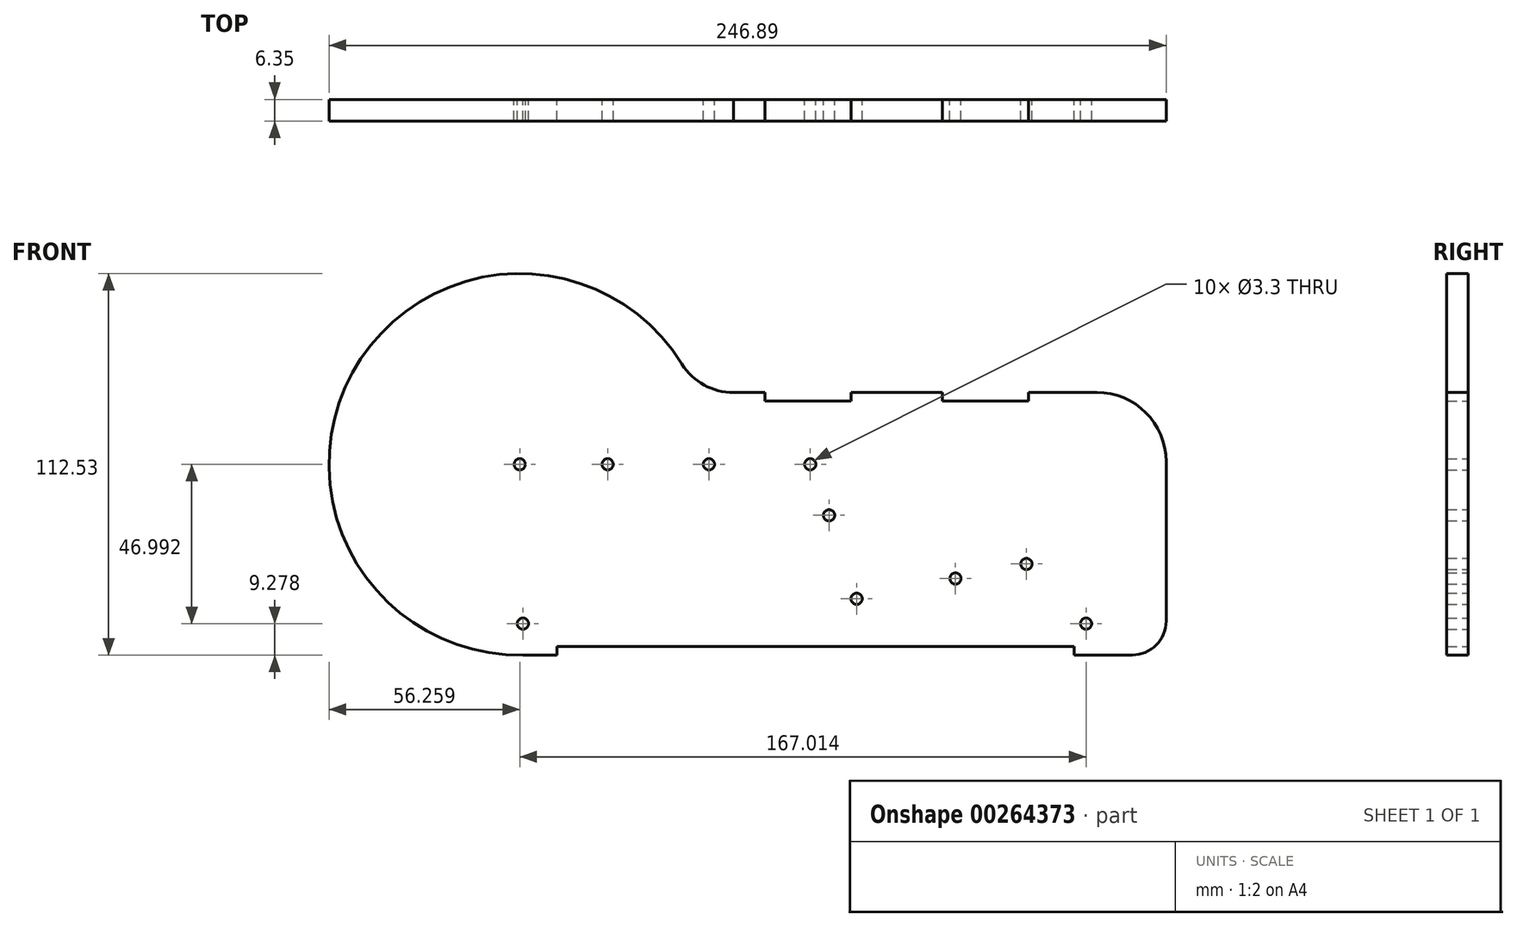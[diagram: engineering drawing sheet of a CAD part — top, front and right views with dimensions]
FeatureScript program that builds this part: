
annotation { "Feature Type Name" : "Feature", "Feature Type Description" : "" }
export const myFeature = defineFeature(function(context is Context, id is Id, definition is map)
    precondition{}
    {
        {
            var Q0;
            Q0=qCreatedBy(makeId("Front.planeOp"),FACE);
            var sketch = newSketch(context, id + "F0", { "sketchPlane" : qUnion([Q0])});
            skCircle(sketch, "E0", {"center": v(-31.53, 0) * mm, "radius": 1.65 * mm});
            skCircle(sketch, "E1", {"center": v(-61.4, 0) * mm, "radius": 1.65 * mm});
            skLineSegment(sketch, "E2.top", {"start": v(-86.4, -56.26) * mm, "end": v(-76.4, -56.26) * mm});
            skLineSegment(sketch, "E2.right", {"start": v(103.3, -10.33) * mm, "end": v(103.3, -46.23) * mm});
            skCircle(sketch, "E3", {"center": v(-87.33, 0) * mm, "radius": 1.65 * mm});
            skCircle(sketch, "E4", {"center": v(-1.66, 0) * mm, "radius": 1.65 * mm});
            skCircle(sketch, "E5", {"center": v(3.89, -15.04) * mm, "radius": 1.65 * mm});
            skCircle(sketch, "E6", {"center": v(41.18, -33.7) * mm, "radius": 1.65 * mm});
            skCircle(sketch, "E7", {"center": v(62.11, -29.4) * mm, "radius": 1.65 * mm});
            skCircle(sketch, "E8", {"center": v(79.68, -47) * mm, "radius": 1.65 * mm});
            skCircle(sketch, "E9", {"center": v(12.02, -39.66) * mm, "radius": 1.65 * mm});
            skLineSegment(sketch, "E10", {"start": v(103.3, -10.33) * mm, "end": v(103.3, 0.8) * mm});
            skLineSegment(sketch, "E11", {"start": v(-24.26, 21.23) * mm, "end": v(-14.95, 21.23) * mm});
            skArc(sketch, "E12.trimOffspring", {"start": v(-39.47, 29.57) * mm, "mid": v(-32.97, 23.4) * mm, "end": v(-24.26, 21.23) * mm});
            skArc(sketch, "E13", {"start": v(103.3, 0.8) * mm, "mid": v(97.31, 15.24) * mm, "end": v(82.87, 21.23) * mm});
            skArc(sketch, "E14.trimOffspring", {"start": v(-39.47, 29.57) * mm, "mid": v(-136.7, 27) * mm, "end": v(-86.4, -56.26) * mm});
            skArc(sketch, "E15.trimOffspring", {"start": v(93.27, -56.26) * mm, "mid": v(100.36, -53.32) * mm, "end": v(103.3, -46.23) * mm});
            skCircle(sketch, "E16", {"center": v(-86.4, -47) * mm, "radius": 1.65 * mm});
            skLineSegment(sketch, "E17", {"start": v(-143.39, 4.78) * mm, "end": v(-143.39, -50.37) * mm, "construction": true});
            skLineSegment(sketch, "E18", {"start": v(-76.4, -56.26) * mm, "end": v(-76.4, -53.72) * mm});
            skLineSegment(sketch, "E19", {"start": v(-76.4, -53.72) * mm, "end": v(76.2, -53.72) * mm});
            skLineSegment(sketch, "E20", {"start": v(76.2, -53.72) * mm, "end": v(76.2, -56.26) * mm});
            skLineSegment(sketch, "E21.trimOffspring", {"start": v(76.2, -56.26) * mm, "end": v(93.27, -56.26) * mm});
            skLineSegment(sketch, "E22", {"start": v(-14.95, 21.23) * mm, "end": v(-14.95, 18.69) * mm});
            skLineSegment(sketch, "E23", {"start": v(-14.95, 18.69) * mm, "end": v(10.45, 18.69) * mm});
            skLineSegment(sketch, "E24", {"start": v(10.45, 18.69) * mm, "end": v(10.45, 21.23) * mm});
            skLineSegment(sketch, "E25", {"start": v(37.3, 21.23) * mm, "end": v(37.3, 18.69) * mm});
            skLineSegment(sketch, "E26", {"start": v(37.3, 18.69) * mm, "end": v(62.7, 18.69) * mm});
            skLineSegment(sketch, "E27", {"start": v(62.7, 18.69) * mm, "end": v(62.7, 21.23) * mm});
            skLineSegment(sketch, "E28.trimOffspring", {"start": v(10.45, 21.23) * mm, "end": v(37.3, 21.23) * mm});
            skLineSegment(sketch, "E29.trimOffspring", {"start": v(62.7, 21.23) * mm, "end": v(82.87, 21.23) * mm});
            skLineSegment(sketch, "E30", {"start": v(79.68, -47) * mm, "end": v(-137.93, -47) * mm, "construction": true});
            skSolve(sketch);
        }
        {
            var Q0;
            Q0 = qSketchRegion(id + "F0", true);
            extrude(context, id + "F1", {"entities" : qUnion([Q0]), "depth" : 6.35 * mm});
        }
    });
